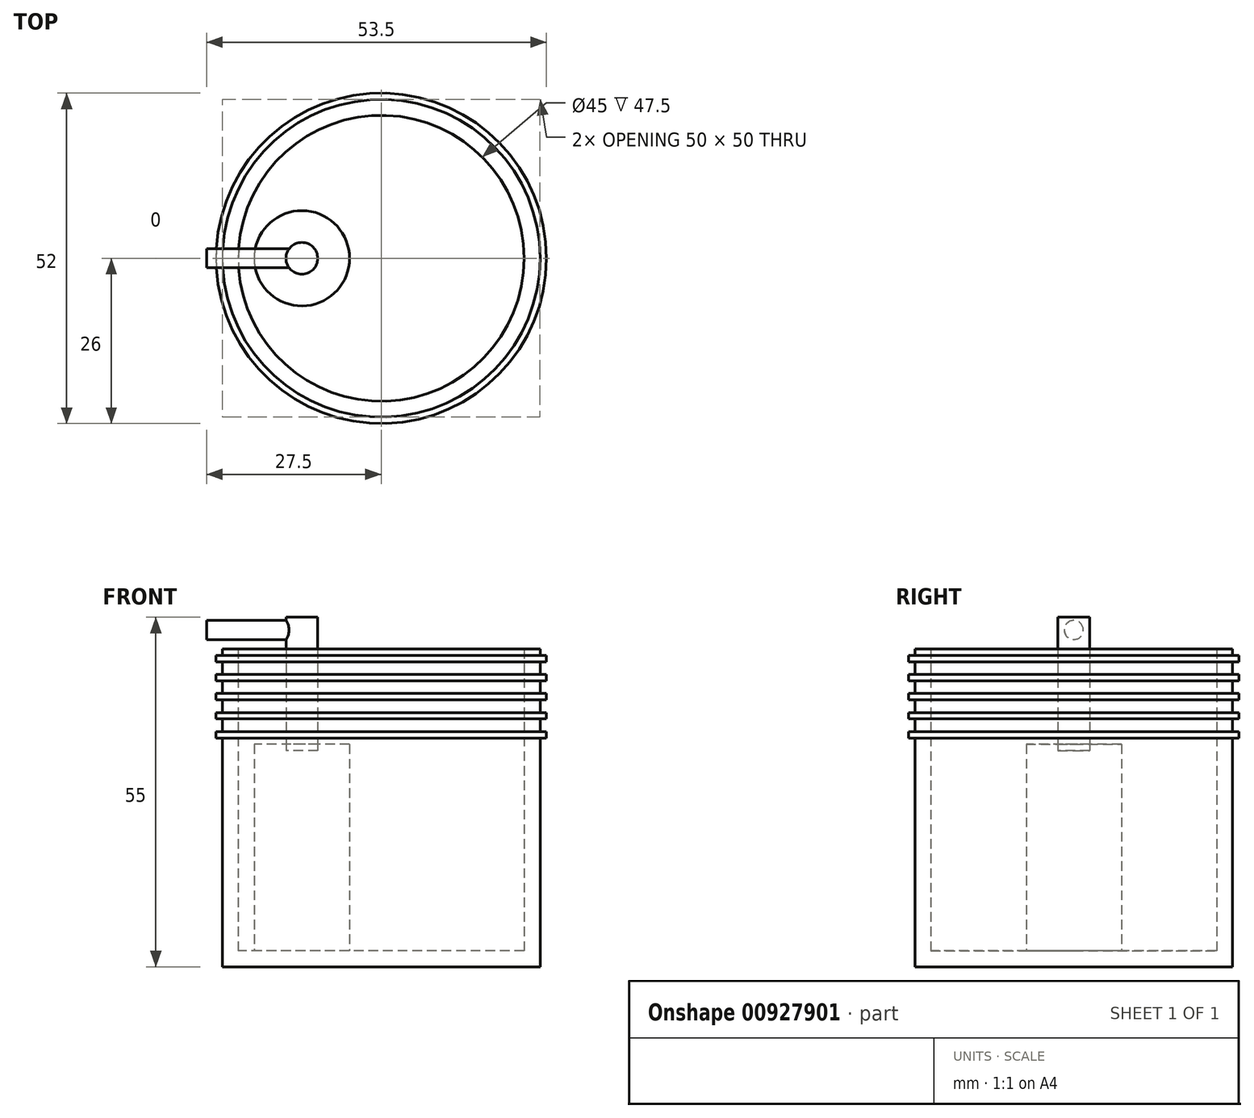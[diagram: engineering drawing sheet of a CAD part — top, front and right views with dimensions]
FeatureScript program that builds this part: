
annotation { "Feature Type Name" : "Feature", "Feature Type Description" : "" }
export const myFeature = defineFeature(function(context is Context, id is Id, definition is map)
    precondition{}
    {
        {
            var Q0;
            Q0=qCreatedBy(makeId("Top.planeOp"),FACE);
            var sketch = newSketch(context, id + "F0", { "sketchPlane" : qUnion([Q0])});
            skCircle(sketch, "E0", {"center": v(0, 0) * mm, "radius": 25 * mm});
            skSolve(sketch);
        }
        {
            var Q0;
            Q0 = qSketchRegion(id + "F0", true);
            extrude(context, id + "F1", {"entities" : qUnion([Q0]), "depth" : 50 * mm, "offsetDistance" : 25 * mm});
        }
        {
            var Q0;
            Q0=makeQuery(id+"F1.opExtrude","CAP_FACE",FACE,{"disambiguationData":[OSD([sQuery(id+"F0.wireOp",EDGE,"E0")])],"isStart":false});
            shell(context, id + "F2", {"entities" : qUnion([Q0]), "thickness" : 2.5 * mm});
        }
        {
            var Q0;
            Q0=qCreatedBy(makeId("Front.planeOp"),FACE);
            var sketch = newSketch(context, id + "F3", { "sketchPlane" : qUnion([Q0])});
            skLineSegment(sketch, "E1", {"start": v(25, 50) * mm, "end": v(25, 0) * mm});
            skLineSegment(sketch, "E2", {"start": v(25, 49) * mm, "end": v(26, 49) * mm});
            skLineSegment(sketch, "E3", {"start": v(26, 49) * mm, "end": v(26, 48) * mm});
            skLineSegment(sketch, "E4", {"start": v(26, 48) * mm, "end": v(25, 48) * mm});
            skLineSegment(sketch, "E5.1.0.0", {"start": v(25, 46) * mm, "end": v(26, 46) * mm});
            skLineSegment(sketch, "E5.1.0.1", {"start": v(26, 46) * mm, "end": v(26, 45) * mm});
            skLineSegment(sketch, "E5.1.0.2", {"start": v(26, 45) * mm, "end": v(25, 45) * mm});
            skLineSegment(sketch, "E5.2.0.0", {"start": v(25, 43) * mm, "end": v(26, 43) * mm});
            skLineSegment(sketch, "E5.2.0.1", {"start": v(26, 43) * mm, "end": v(26, 42) * mm});
            skLineSegment(sketch, "E5.2.0.2", {"start": v(26, 42) * mm, "end": v(25, 42) * mm});
            skLineSegment(sketch, "E5.3.0.0", {"start": v(25, 40) * mm, "end": v(26, 40) * mm});
            skLineSegment(sketch, "E5.3.0.1", {"start": v(26, 40) * mm, "end": v(26, 39) * mm});
            skLineSegment(sketch, "E5.3.0.2", {"start": v(26, 39) * mm, "end": v(25, 39) * mm});
            skLineSegment(sketch, "E5.4.0.0", {"start": v(25, 37) * mm, "end": v(26, 37) * mm});
            skLineSegment(sketch, "E5.4.0.1", {"start": v(26, 37) * mm, "end": v(26, 36) * mm});
            skLineSegment(sketch, "E5.4.0.2", {"start": v(26, 36) * mm, "end": v(25, 36) * mm});
            skLineSegment(sketch, "E5.direction1", {"start": v(25, 49) * mm, "end": v(25, 46) * mm, "construction": true});
            skLineSegment(sketch, "E6", {"start": v(0, 0) * mm, "end": v(0, 50) * mm, "construction": true});
            skSolve(sketch);
        }
        {
            var Q0;
            Q0 = qSketchRegion(id + "F3", true);
            var Q1;
            Q1=sQuery(id+"F3.wireOp",EDGE,"E6");
            revolve(context, id + "F4", {"operationType" : NewBodyOperationType.ADD, "surfaceOperationType" : NewSurfaceOperationType.NEW, "entities" : qUnion([Q0]), "axis" : qUnion([Q1]), "revolveType" : RevolveType.FULL});
        }
        {
            var Q0;
            Q0=qCreatedBy(makeId("Top.planeOp"),FACE);
            var sketch = newSketch(context, id + "F5", { "sketchPlane" : qUnion([Q0])});
            skCircle(sketch, "E7", {"center": v(-12.5, 0) * mm, "radius": 7.5 * mm});
            skLineSegment(sketch, "E8", {"start": v(0, 0) * mm, "end": v(-25, 0) * mm, "construction": true});
            skSolve(sketch);
        }
        {
            var Q0;
            Q0 = qSketchRegion(id + "F5", true);
            extrude(context, id + "F6", {"entities" : qUnion([Q0]), "depth" : 35 * mm, "offsetDistance" : 25 * mm, "hasSecondDirection" : true, "secondDirectionOppositeDirection" : false, "secondDirectionDepth" : 2.5 * mm});
        }
        {
            var Q0;
            Q0=makeQuery(id+"F6.opExtrude","CAP_FACE",FACE,{"disambiguationData":[OSD([sQuery(id+"F5.wireOp",EDGE,"E7")])],"isStart":false});
            var sketch = newSketch(context, id + "F7", { "sketchPlane" : qUnion([Q0])});
            skCircle(sketch, "E9", {"center": v(-12.5, 0) * mm, "radius": 2.5 * mm});
            skSolve(sketch);
        }
        {
            var Q0;
            Q0 = qSketchRegion(id + "F7", true);
            extrude(context, id + "F8", {"entities" : qUnion([Q0]), "depth" : 20 * mm, "offsetDistance" : 25 * mm, "hasSecondDirection" : true, "secondDirectionOppositeDirection" : true, "secondDirectionDepth" : 1 * mm});
        }
        {
            var Q0;
            Q0=makeQuery(id+"F8.opExtrude","SWEPT_BODY",BODY,{"disambiguationData":[OSD([sQuery(id+"F7.wireOp",EDGE,"E9")])]});
            var Q1;
            Q1=makeQuery(id+"F6.opExtrude","SWEPT_BODY",BODY,{"disambiguationData":[OSD([sQuery(id+"F5.wireOp",EDGE,"E7")])]});
            booleanBodies(context, id + "F9", {"operationType" : BooleanOperationType.SUBTRACTION, "tools" : qUnion([Q0]), "targets" : qUnion([Q1]), "keepTools" : true});
        }
        {
            var Q0;
            Q0=qCreatedBy(makeId("Right.planeOp"),FACE);
            cPlane(context, id + "F10", {"entities" : qUnion([Q0]), "cplaneType" : CPlaneType.OFFSET, "offset" : 12.5 * mm, "oppositeDirection" : true, "width" : 150 * mm, "height" : 150 * mm});
        }
        {
            var Q0;
            Q0=qCreatedBy(id+"F10.planeOp",FACE);
            var sketch = newSketch(context, id + "F11", { "sketchPlane" : qUnion([Q0])});
            skCircle(sketch, "E10", {"center": v(0, 53) * mm, "radius": 1.5 * mm});
            skSolve(sketch);
        }
        {
            var Q0;
            Q0 = qSketchRegion(id + "F11", true);
            extrude(context, id + "F12", {"entities" : qUnion([Q0]), "operationType" : NewBodyOperationType.ADD, "oppositeDirection" : true, "depth" : 15 * mm, "offsetDistance" : 25 * mm});
        }
    });
